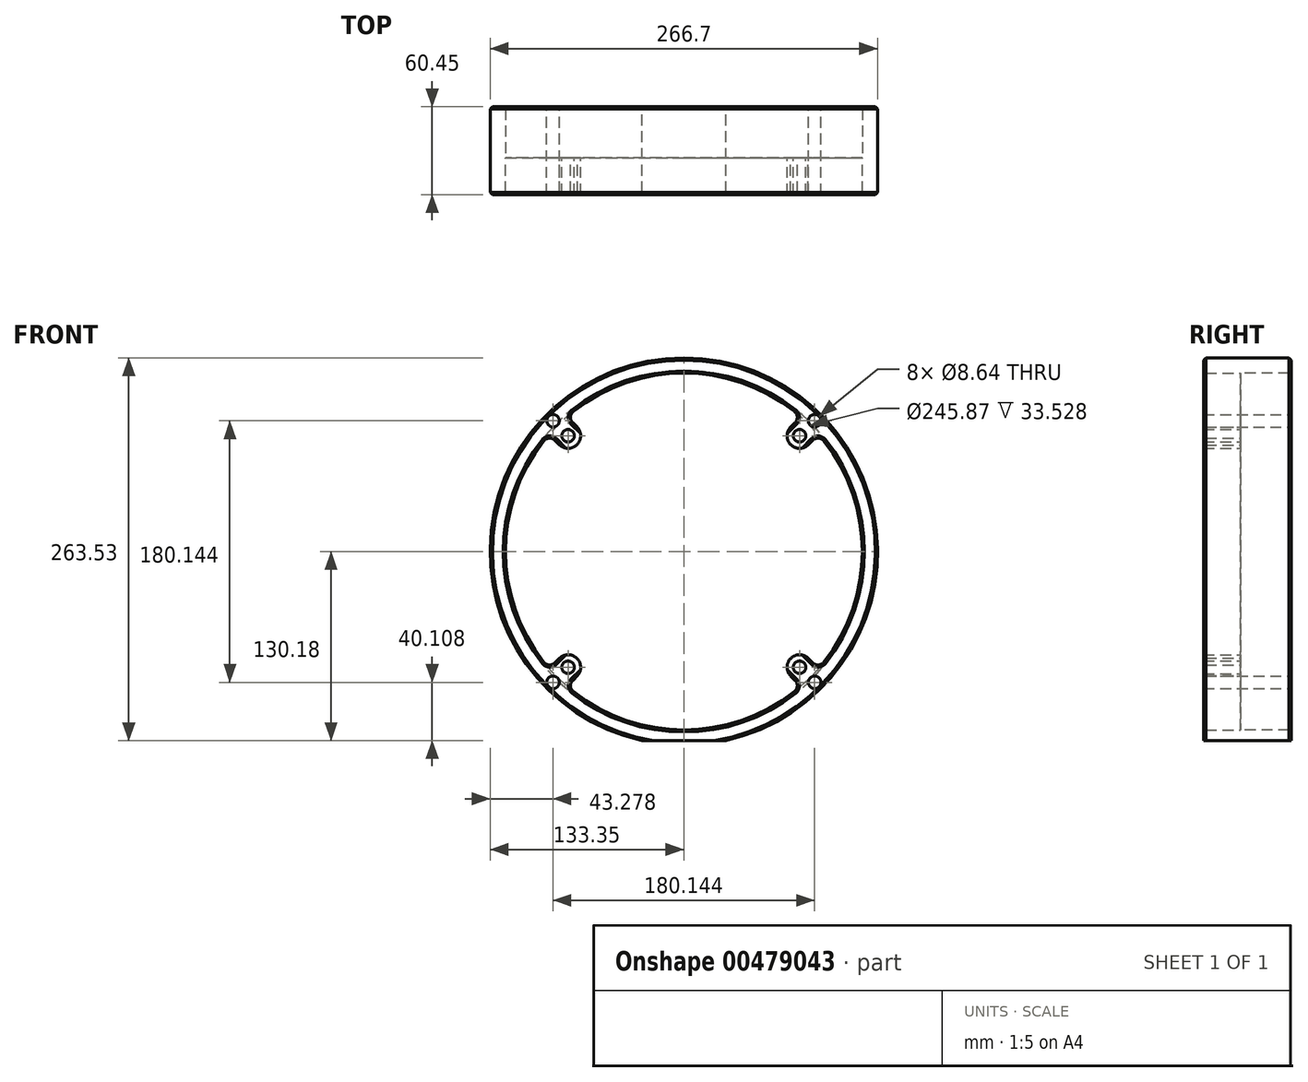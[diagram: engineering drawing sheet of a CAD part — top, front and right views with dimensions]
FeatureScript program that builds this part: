
annotation { "Feature Type Name" : "Feature", "Feature Type Description" : "" }
export const myFeature = defineFeature(function(context is Context, id is Id, definition is map)
    precondition{}
    {
        {
            var Q0;
            Q0=qCreatedBy(makeId("Front.planeOp"),FACE);
            var sketch = newSketch(context, id + "F0", { "sketchPlane" : qUnion([Q0])});
            skCircle(sketch, "E0", {"center": v(0, 0) * mm, "radius": 112.71 * mm, "construction": true});
            skLineSegment(sketch, "E1", {"start": v(0, 0) * mm, "end": v(100.3, 100.3) * mm, "construction": true});
            skCircle(sketch, "E2", {"center": v(79.7, 79.7) * mm, "radius": 4.32 * mm});
            skCircle(sketch, "E3.1.0", {"center": v(-79.7, 79.7) * mm, "radius": 4.32 * mm});
            skCircle(sketch, "E3.2.0", {"center": v(-79.7, -79.7) * mm, "radius": 4.32 * mm});
            skCircle(sketch, "E3.3.0", {"center": v(79.7, -79.7) * mm, "radius": 4.32 * mm});
            skArc(sketch, "E4", {"start": v(73.83, 86.03) * mm, "mid": v(73.57, 73.61) * mm, "end": v(86, 73.79) * mm});
            skArc(sketch, "E5", {"start": v(80.52, 92.73) * mm, "mid": v(0, 122.8) * mm, "end": v(-80.52, 92.73) * mm});
            skCircle(sketch, "E6", {"center": v(0, 0) * mm, "radius": 133.35 * mm, "construction": true});
            skArc(sketch, "E7", {"start": v(28.93, -130.18) * mm, "mid": v(0, 133.35) * mm, "end": v(-28.93, -130.18) * mm});
            skLineSegment(sketch, "E8", {"start": v(73.36, 85.57) * mm, "end": v(80.52, 92.73) * mm});
            skLineSegment(sketch, "E9", {"start": v(85.61, 73.4) * mm, "end": v(92.73, 80.52) * mm});
            skLineSegment(sketch, "E10.trimOffspring", {"start": v(88, 100.2) * mm, "end": v(88, 100.2) * mm});
            skLineSegment(sketch, "E11.trimOffspring", {"start": v(100.2, 88) * mm, "end": v(100.59, 88.38) * mm});
            skLineSegment(sketch, "E12.1.0", {"start": v(-85.57, 73.36) * mm, "end": v(-92.73, 80.52) * mm});
            skLineSegment(sketch, "E12.1.1", {"start": v(-73.4, 85.61) * mm, "end": v(-80.52, 92.73) * mm});
            skArc(sketch, "E12.1.2", {"start": v(-86.03, 73.83) * mm, "mid": v(-73.61, 73.57) * mm, "end": v(-73.79, 86) * mm});
            skLineSegment(sketch, "E12.2.0", {"start": v(-73.36, -85.57) * mm, "end": v(-80.52, -92.73) * mm});
            skLineSegment(sketch, "E12.2.1", {"start": v(-85.61, -73.4) * mm, "end": v(-92.73, -80.52) * mm});
            skArc(sketch, "E12.2.2", {"start": v(-73.83, -86.03) * mm, "mid": v(-73.57, -73.61) * mm, "end": v(-86, -73.79) * mm});
            skLineSegment(sketch, "E12.3.0", {"start": v(85.57, -73.36) * mm, "end": v(92.73, -80.52) * mm});
            skLineSegment(sketch, "E12.3.1", {"start": v(73.4, -85.61) * mm, "end": v(80.52, -92.73) * mm});
            skArc(sketch, "E12.3.2", {"start": v(86.03, -73.83) * mm, "mid": v(73.61, -73.57) * mm, "end": v(73.79, -86) * mm});
            skArc(sketch, "E13.trimOffspring", {"start": v(-92.73, 80.52) * mm, "mid": v(-122.8, 0) * mm, "end": v(-92.73, -80.52) * mm});
            skArc(sketch, "E14.trimOffspring", {"start": v(-80.52, -92.73) * mm, "mid": v(0, -122.8) * mm, "end": v(80.52, -92.73) * mm});
            skArc(sketch, "E15.trimOffspring", {"start": v(92.73, -80.52) * mm, "mid": v(122.8, 0) * mm, "end": v(92.73, 80.52) * mm});
            skLineSegment(sketch, "E16", {"start": v(-28.93, -130.18) * mm, "end": v(28.93, -130.18) * mm});
            skSolve(sketch);
        }
        {
            var Q0;
            Q0=makeQuery(id+"F0.imprint","IMPRINT",FACE,{"disambiguationData":[TD([[makeQuery(id+"F0.imprint","IMPRINT",EDGE,{"derivedFrom":sQuery(id+"F0.wireOp",EDGE,"E2")}),-1.0]])]});
            extrude(context, id + "F1", {"entities" : qUnion([Q0]), "depth" : 25.4 * mm});
        }
        {
            var Q0;
            Q0=makeQuery(id+"F1.opExtrude","CAP_FACE",FACE,{"disambiguationData":[OSD([sQuery(id+"F0.wireOp",EDGE,"E2"),sQuery(id+"F0.wireOp",EDGE,"E3.1.0"),sQuery(id+"F0.wireOp",EDGE,"E3.2.0"),sQuery(id+"F0.wireOp",EDGE,"E3.3.0"),sQuery(id+"F0.wireOp",EDGE,"E4"),sQuery(id+"F0.wireOp",EDGE,"E5"),sQuery(id+"F0.wireOp",EDGE,"E7"),sQuery(id+"F0.wireOp",EDGE,"DTZbBTyo-910V-rojo-BSng-KiafCCvbkYSo"),sQuery(id+"F0.wireOp",EDGE,"GR1iSiWp-XWoq-ONjd-FFDE-OR4YaewtADHj"),sQuery(id+"F0.wireOp",EDGE,"E8"),sQuery(id+"F0.wireOp",EDGE,"E9"),sQuery(id+"F0.wireOp",EDGE,"E12.1.0"),sQuery(id+"F0.wireOp",EDGE,"E12.1.1"),sQuery(id+"F0.wireOp",EDGE,"E12.1.2"),sQuery(id+"F0.wireOp",EDGE,"E12.2.0"),sQuery(id+"F0.wireOp",EDGE,"E12.2.1"),sQuery(id+"F0.wireOp",EDGE,"E12.2.2"),sQuery(id+"F0.wireOp",EDGE,"E12.3.0"),sQuery(id+"F0.wireOp",EDGE,"E12.3.1"),sQuery(id+"F0.wireOp",EDGE,"E12.3.2"),sQuery(id+"F0.wireOp",EDGE,"E13.trimOffspring"),sQuery(id+"F0.wireOp",EDGE,"E14.trimOffspring"),sQuery(id+"F0.wireOp",EDGE,"E15.trimOffspring")])],"isStart":true});
            var sketch = newSketch(context, id + "F2", { "sketchPlane" : qUnion([Q0])});
            skCircle(sketch, "E17", {"center": v(0, 0) * mm, "radius": 136.93 * mm});
            skCircle(sketch, "E18", {"center": v(0, 0) * mm, "radius": 122.94 * mm});
            skSolve(sketch);
        }
        {
            var Q0;
            Q0=makeQuery(id+"F2.imprint","IMPRINT",FACE,{"disambiguationData":[TD([[makeQuery(id+"F2.imprint","IMPRINT",EDGE,{"derivedFrom":sQuery(id+"F2.wireOp",EDGE,"E18")}),-1.0]])]});
            extrude(context, id + "F3", {"entities" : qUnion([Q0]), "operationType" : NewBodyOperationType.ADD, "depth" : 35.05 * mm});
        }
        {
            var Q0;
            Q0=makeQuery(id+"F3.opExtrude","CAP_FACE",FACE,{"disambiguationData":[OSD([sQuery(id+"F0.wireOp",EDGE,"E7"),sQuery(id+"F0.wireOp",EDGE,"DTZbBTyo-910V-rojo-BSng-KiafCCvbkYSo"),sQuery(id+"F0.wireOp",EDGE,"GR1iSiWp-XWoq-ONjd-FFDE-OR4YaewtADHj"),sQuery(id+"F2.wireOp",EDGE,"E17")])],"isStart":false});
            var sketch = newSketch(context, id + "F4", { "sketchPlane" : qUnion([Q0])});
            skCircle(sketch, "E19", {"center": v(0, 0) * mm, "radius": 127.38 * mm, "construction": true});
            skCircle(sketch, "E20", {"center": v(-90.07, 90.07) * mm, "radius": 4.32 * mm});
            skCircle(sketch, "E21.1.0", {"center": v(-90.07, -90.07) * mm, "radius": 4.32 * mm});
            skCircle(sketch, "E21.2.0", {"center": v(90.07, -90.07) * mm, "radius": 4.32 * mm});
            skCircle(sketch, "E21.3.0", {"center": v(90.07, 90.07) * mm, "radius": 4.32 * mm});
            skSolve(sketch);
        }
        {
            var Q0;
            Q0=makeQuery(id+"F4.imprint","IMPRINT",FACE,{"disambiguationData":[TD([[makeQuery(id+"F4.imprint","IMPRINT",EDGE,{"derivedFrom":sQuery(id+"F4.wireOp",EDGE,"E20")}),1.0]])]});
            var Q1;
            Q1=makeQuery(id+"F4.imprint","IMPRINT",FACE,{"disambiguationData":[TD([[makeQuery(id+"F4.imprint","IMPRINT",EDGE,{"derivedFrom":sQuery(id+"F4.wireOp",EDGE,"E21.3.0")}),1.0]])]});
            var Q2;
            Q2=makeQuery(id+"F4.imprint","IMPRINT",FACE,{"disambiguationData":[TD([[makeQuery(id+"F4.imprint","IMPRINT",EDGE,{"derivedFrom":sQuery(id+"F4.wireOp",EDGE,"E21.2.0")}),1.0]])]});
            var Q3;
            Q3=makeQuery(id+"F4.imprint","IMPRINT",FACE,{"disambiguationData":[TD([[makeQuery(id+"F4.imprint","IMPRINT",EDGE,{"derivedFrom":sQuery(id+"F4.wireOp",EDGE,"E21.1.0")}),1.0]])]});
            extrude(context, id + "F5", {"entities" : qUnion([Q0, Q1, Q2, Q3]), "operationType" : NewBodyOperationType.REMOVE, "endBound" : BoundingType.THROUGH_ALL, "oppositeDirection" : true, "depth" : 25.4 * mm});
        }
        {
            var Q0;
            Q0=makeQuery(id+"F1.opExtrude","SWEPT_EDGE",EDGE,{"disambiguationData":[OSD([sQuery(id+"F0.wireOp",EDGE,"E5"),sQuery(id+"F0.wireOp",EDGE,"E12.1.1")])]});
            var Q1;
            Q1=makeQuery(id+"F1.opExtrude","SWEPT_EDGE",EDGE,{"disambiguationData":[OSD([sQuery(id+"F0.wireOp",EDGE,"E12.1.0"),sQuery(id+"F0.wireOp",EDGE,"E13.trimOffspring")])]});
            var Q2;
            Q2=makeQuery(id+"F1.opExtrude","SWEPT_EDGE",EDGE,{"disambiguationData":[OSD([sQuery(id+"F0.wireOp",EDGE,"E5"),sQuery(id+"F0.wireOp",EDGE,"E8")])]});
            var Q3;
            Q3=makeQuery(id+"F1.opExtrude","SWEPT_EDGE",EDGE,{"disambiguationData":[OSD([sQuery(id+"F0.wireOp",EDGE,"E9"),sQuery(id+"F0.wireOp",EDGE,"E15.trimOffspring")])]});
            var Q4;
            Q4=makeQuery(id+"F1.opExtrude","SWEPT_EDGE",EDGE,{"disambiguationData":[OSD([sQuery(id+"F0.wireOp",EDGE,"E12.3.0"),sQuery(id+"F0.wireOp",EDGE,"E15.trimOffspring")])]});
            var Q5;
            Q5=makeQuery(id+"F1.opExtrude","SWEPT_EDGE",EDGE,{"disambiguationData":[OSD([sQuery(id+"F0.wireOp",EDGE,"E12.3.1"),sQuery(id+"F0.wireOp",EDGE,"E14.trimOffspring")])]});
            var Q6;
            Q6=makeQuery(id+"F1.opExtrude","SWEPT_EDGE",EDGE,{"disambiguationData":[OSD([sQuery(id+"F0.wireOp",EDGE,"E12.2.0"),sQuery(id+"F0.wireOp",EDGE,"E14.trimOffspring")])]});
            var Q7;
            Q7=makeQuery(id+"F1.opExtrude","SWEPT_EDGE",EDGE,{"disambiguationData":[OSD([sQuery(id+"F0.wireOp",EDGE,"E12.2.1"),sQuery(id+"F0.wireOp",EDGE,"E13.trimOffspring")])]});
            fillet(context, id + "F6", {"entities" : qUnion([Q0, Q1, Q2, Q3, Q4, Q5, Q6, Q7]), "radius" : 5.08 * mm, "tangentPropagation" : true, "allowEdgeOverflow" : false});
        }
        {
            var Q0;
            Q0=makeQuery(id+"F1.opExtrude","CAP_EDGE",EDGE,{"disambiguationData":[OSD([sQuery(id+"F0.wireOp",EDGE,"E7")])],"isStart":false});
            var Q1;
            Q1=makeQuery(id+"F1.opExtrude","CAP_EDGE",EDGE,{"disambiguationData":[OSD([sQuery(id+"F0.wireOp",EDGE,"E13.trimOffspring")])],"isStart":false});
            var Q2;
            Q2=makeQuery(id+"F3.opExtrude","CAP_EDGE",EDGE,{"disambiguationData":[OSD([sQuery(id+"F0.wireOp",EDGE,"E7")])],"isStart":false});
            var Q3;
            Q3=makeQuery(id+"F3.opExtrude","CAP_EDGE",EDGE,{"disambiguationData":[OSD([sQuery(id+"F2.wireOp",EDGE,"E18")])],"isStart":false});
            var Q4;
            Q4=makeQuery(id+"F1.opExtrude","CAP_EDGE",EDGE,{"disambiguationData":[OSD([sQuery(id+"F0.wireOp",EDGE,"E14.trimOffspring")])],"isStart":false});
            var Q5;
            Q5=makeQuery(id+"F1.opExtrude","CAP_EDGE",EDGE,{"disambiguationData":[OSD([sQuery(id+"F0.wireOp",EDGE,"E15.trimOffspring")])],"isStart":false});
            var Q6;
            Q6=makeQuery(id+"F1.opExtrude","CAP_EDGE",EDGE,{"disambiguationData":[OSD([sQuery(id+"F0.wireOp",EDGE,"E5")])],"isStart":false});
            chamfer(context, id + "F7", {"entities" : qUnion([Q0, Q1, Q2, Q3, Q4, Q5, Q6]), "width" : 1.52 * mm, "tangentPropagation" : true});
        }
    });
